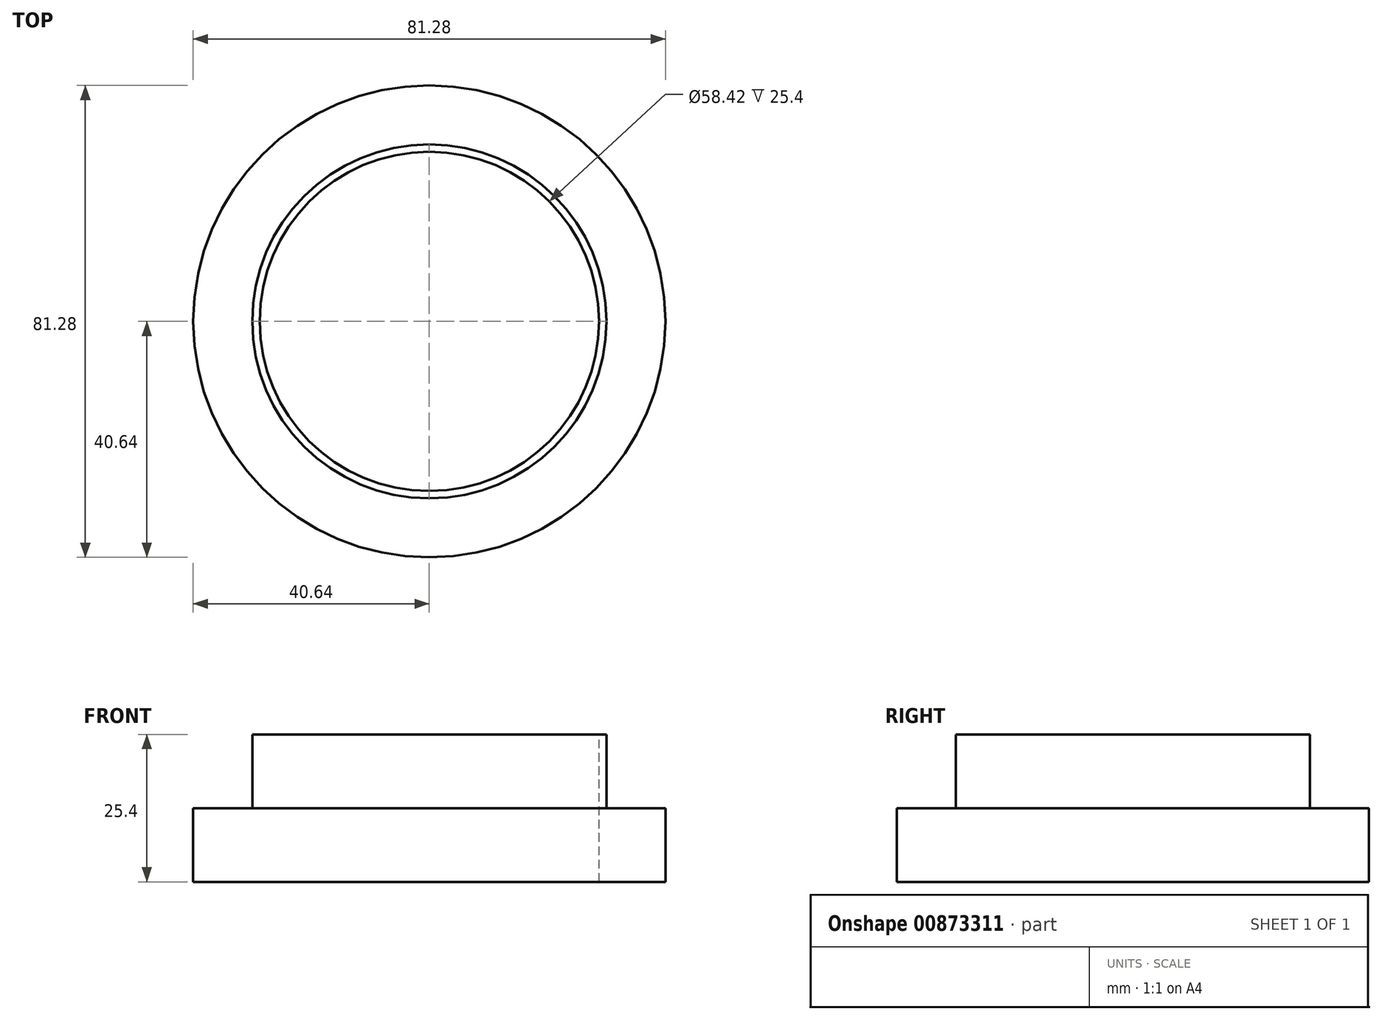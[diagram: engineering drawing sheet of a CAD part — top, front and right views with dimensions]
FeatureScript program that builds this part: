
annotation { "Feature Type Name" : "Feature", "Feature Type Description" : "" }
export const myFeature = defineFeature(function(context is Context, id is Id, definition is map)
    precondition{}
    {
        {
            var Q0;
            Q0=qCreatedBy(makeId("Top.planeOp"),FACE);
            var sketch = newSketch(context, id + "F0", { "sketchPlane" : qUnion([Q0])});
            skCircle(sketch, "E0", {"center": v(0, 0) * mm, "radius": 40.64 * mm});
            skCircle(sketch, "E1", {"center": v(0, 0) * mm, "radius": 29.21 * mm});
            skSolve(sketch);
        }
        {
            var Q0;
            Q0=makeQuery(id+"F0.imprint","IMPRINT",FACE,{"disambiguationData":[TD([[makeQuery(id+"F0.imprint","IMPRINT",EDGE,{"derivedFrom":sQuery(id+"F0.wireOp",EDGE,"E0")}),1.0]])]});
            extrude(context, id + "F1", {"entities" : qUnion([Q0]), "depth" : -10.16 * mm, "offsetDistance" : 25.4 * mm});
        }
        {
            var Q0;
            Q0=makeQuery(id+"F1.opExtrude","CAP_FACE",FACE,{"disambiguationData":[OSD([sQuery(id+"F0.wireOp",EDGE,"E0"),sQuery(id+"F0.wireOp",EDGE,"E1")])],"isStart":true});
            extrude(context, id + "F2", {"entities" : qUnion([Q0]), "operationType" : NewBodyOperationType.ADD, "depth" : 2.54 * mm, "offsetDistance" : 25.4 * mm});
        }
        {
            var Q0;
            Q0=qCreatedBy(makeId("Top.planeOp"),FACE);
            var sketch = newSketch(context, id + "F3", { "sketchPlane" : qUnion([Q0])});
            skCircle(sketch, "E2", {"center": v(0, 0) * mm, "radius": 30.48 * mm});
            skCircle(sketch, "E3", {"center": v(0, 0) * mm, "radius": 29.21 * mm});
            skSolve(sketch);
        }
        {
            var Q0;
            Q0 = qSketchRegion(id + "F3", true);
            extrude(context, id + "F4", {"entities" : qUnion([Q0]), "operationType" : NewBodyOperationType.ADD, "depth" : 15.24 * mm, "offsetDistance" : 25.4 * mm});
        }
    });
